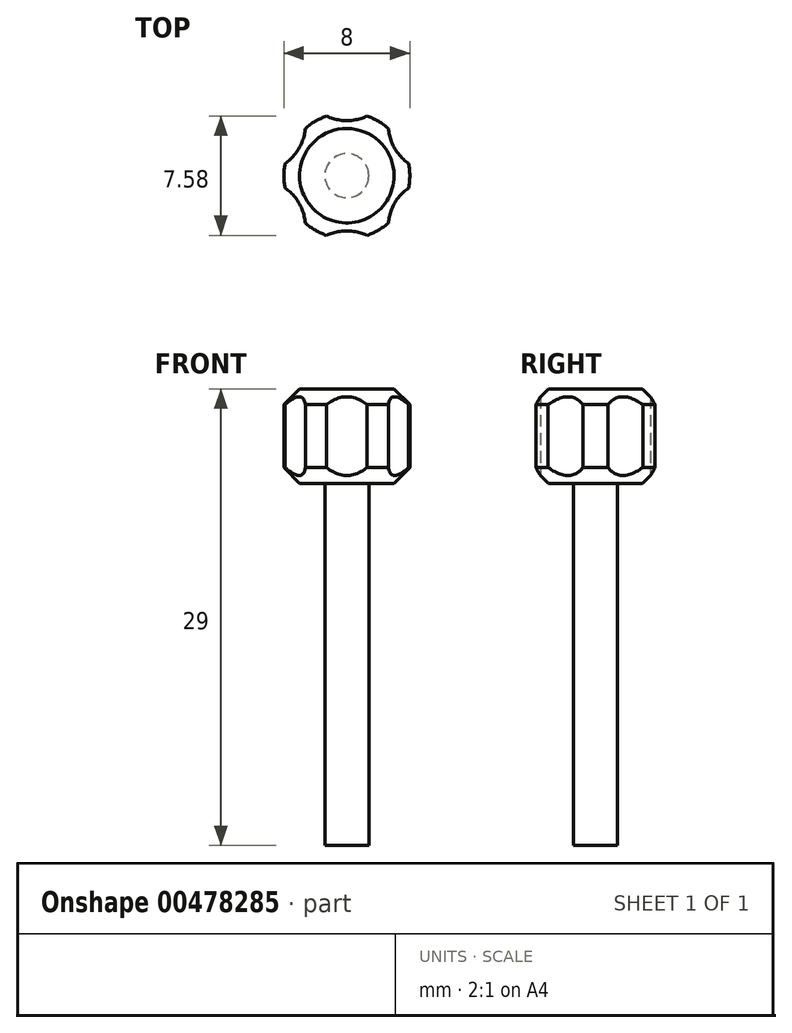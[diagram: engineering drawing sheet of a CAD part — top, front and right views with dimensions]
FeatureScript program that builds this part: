
annotation { "Feature Type Name" : "Feature", "Feature Type Description" : "" }
export const myFeature = defineFeature(function(context is Context, id is Id, definition is map)
    precondition{}
    {
        {
            var Q0;
            Q0=qCreatedBy(makeId("Top.planeOp"),FACE);
            var sketch = newSketch(context, id + "F0", { "sketchPlane" : qUnion([Q0])});
            skCircle(sketch, "E0", {"center": v(0, 0) * mm, "radius": 4 * mm});
            skCircle(sketch, "E1", {"center": v(0, 0) * mm, "radius": 1.4 * mm});
            skCircle(sketch, "E2", {"center": v(0, 6.5) * mm, "radius": 3 * mm});
            skCircle(sketch, "E3.1.0", {"center": v(-5.63, 3.25) * mm, "radius": 3 * mm});
            skCircle(sketch, "E3.2.0", {"center": v(-5.63, -3.25) * mm, "radius": 3 * mm});
            skCircle(sketch, "E3.3.0", {"center": v(0, -6.5) * mm, "radius": 3 * mm});
            skCircle(sketch, "E3.4.0", {"center": v(5.63, -3.25) * mm, "radius": 3 * mm});
            skCircle(sketch, "E3.5.0", {"center": v(5.63, 3.25) * mm, "radius": 3 * mm});
            skSolve(sketch);
        }
        {
            var Q0;
            Q0=makeQuery(id+"F0.imprint","IMPRINT",FACE,{"disambiguationData":[TD([[makeQuery(id+"F0.imprint","IMPRINT",EDGE,{"derivedFrom":sQuery(id+"F0.wireOp",EDGE,"E1")}),-1.0]])]});
            var Q1;
            Q1=makeQuery(id+"F0.imprint","IMPRINT",FACE,{"disambiguationData":[TD([[makeQuery(id+"F0.imprint","IMPRINT",EDGE,{"derivedFrom":sQuery(id+"F0.wireOp",EDGE,"E1")}),1.0]])]});
            var Q2;
            {var subQ0=sQuery(id+"F0.wireOp",EDGE,"E2");var subQ1=sQuery(id+"F0.wireOp",EDGE,"E0");var subQ2=makeQuery(id+"F0.imprint","INTERSECT",VERTEX,{"disambiguationData":[OD(0.0)],"derivedFrom":[subQ1,subQ0]});Q2=makeQuery(id+"F0.imprint","IMPRINT",FACE,{"disambiguationData":[TD([[makeQuery(id+"F0.imprint","IMPRINT",EDGE,{"disambiguationData":[TD([[subQ2,-1.0]])],"derivedFrom":subQ1}),1.0]])]});}
            var Q3;
            {var subQ0=sQuery(id+"F0.wireOp",EDGE,"E3.5.0");var subQ1=sQuery(id+"F0.wireOp",EDGE,"E0");var subQ2=makeQuery(id+"F0.imprint","INTERSECT",VERTEX,{"disambiguationData":[OD(0.0)],"derivedFrom":[subQ1,subQ0]});Q3=makeQuery(id+"F0.imprint","IMPRINT",FACE,{"disambiguationData":[TD([[makeQuery(id+"F0.imprint","IMPRINT",EDGE,{"disambiguationData":[TD([[subQ2,1.0]])],"derivedFrom":subQ1}),1.0]])]});}
            var Q4;
            {var subQ0=sQuery(id+"F0.wireOp",EDGE,"E3.4.0");var subQ1=sQuery(id+"F0.wireOp",EDGE,"E0");var subQ2=makeQuery(id+"F0.imprint","INTERSECT",VERTEX,{"disambiguationData":[OD(0.0)],"derivedFrom":[subQ1,subQ0]});Q4=makeQuery(id+"F0.imprint","IMPRINT",FACE,{"disambiguationData":[TD([[makeQuery(id+"F0.imprint","IMPRINT",EDGE,{"disambiguationData":[TD([[subQ2,-1.0]])],"derivedFrom":subQ1}),1.0]])]});}
            var Q5;
            {var subQ0=sQuery(id+"F0.wireOp",EDGE,"E3.3.0");var subQ1=sQuery(id+"F0.wireOp",EDGE,"E0");var subQ2=makeQuery(id+"F0.imprint","INTERSECT",VERTEX,{"disambiguationData":[OD(0.0)],"derivedFrom":[subQ1,subQ0]});Q5=makeQuery(id+"F0.imprint","IMPRINT",FACE,{"disambiguationData":[TD([[makeQuery(id+"F0.imprint","IMPRINT",EDGE,{"disambiguationData":[TD([[subQ2,-1.0]])],"derivedFrom":subQ1}),1.0]])]});}
            var Q6;
            {var subQ0=sQuery(id+"F0.wireOp",EDGE,"E3.2.0");var subQ1=sQuery(id+"F0.wireOp",EDGE,"E0");var subQ2=makeQuery(id+"F0.imprint","INTERSECT",VERTEX,{"disambiguationData":[OD(0.0)],"derivedFrom":[subQ1,subQ0]});Q6=makeQuery(id+"F0.imprint","IMPRINT",FACE,{"disambiguationData":[TD([[makeQuery(id+"F0.imprint","IMPRINT",EDGE,{"disambiguationData":[TD([[subQ2,-1.0]])],"derivedFrom":subQ1}),1.0]])]});}
            var Q7;
            {var subQ0=sQuery(id+"F0.wireOp",EDGE,"E3.1.0");var subQ1=sQuery(id+"F0.wireOp",EDGE,"E0");var subQ2=makeQuery(id+"F0.imprint","INTERSECT",VERTEX,{"disambiguationData":[OD(0.0)],"derivedFrom":[subQ1,subQ0]});Q7=makeQuery(id+"F0.imprint","IMPRINT",FACE,{"disambiguationData":[TD([[makeQuery(id+"F0.imprint","IMPRINT",EDGE,{"disambiguationData":[TD([[subQ2,-1.0]])],"derivedFrom":subQ1}),1.0]])]});}
            extrude(context, id + "F1", {"entities" : qUnion([Q0, Q1, Q2, Q3, Q4, Q5, Q6, Q7]), "depth" : 6 * mm});
        }
        {
            var Q0;
            Q0=makeQuery(id+"F1.opExtrude","CAP_EDGE",EDGE,{"disambiguationData":[OSD([sQuery(id+"F0.wireOp",EDGE,"E0")])],"isStart":false});
            var Q1;
            Q1=makeQuery(id+"F1.opExtrude","CAP_EDGE",EDGE,{"disambiguationData":[OSD([sQuery(id+"F0.wireOp",EDGE,"E0")])],"isStart":true});
            chamfer(context, id + "F2", {"entities" : qUnion([Q0, Q1]), "width" : 1 * mm, "tangentPropagation" : true});
        }
        {
            var Q0;
            {var subQ0=sQuery(id+"F0.wireOp",EDGE,"E3.3.0");var subQ1=sQuery(id+"F0.wireOp",EDGE,"E0");var subQ2=makeQuery(id+"F0.imprint","INTERSECT",VERTEX,{"disambiguationData":[OD(0.0)],"derivedFrom":[subQ1,subQ0]});Q0=makeQuery(id+"F0.imprint","IMPRINT",FACE,{"disambiguationData":[TD([[makeQuery(id+"F0.imprint","IMPRINT",EDGE,{"disambiguationData":[TD([[subQ2,-1.0]])],"derivedFrom":subQ1}),1.0]])]});}
            var Q1;
            {var subQ0=sQuery(id+"F0.wireOp",EDGE,"E3.2.0");var subQ1=sQuery(id+"F0.wireOp",EDGE,"E0");var subQ2=makeQuery(id+"F0.imprint","INTERSECT",VERTEX,{"disambiguationData":[OD(0.0)],"derivedFrom":[subQ1,subQ0]});Q1=makeQuery(id+"F0.imprint","IMPRINT",FACE,{"disambiguationData":[TD([[makeQuery(id+"F0.imprint","IMPRINT",EDGE,{"disambiguationData":[TD([[subQ2,-1.0]])],"derivedFrom":subQ1}),1.0]])]});}
            var Q2;
            {var subQ0=sQuery(id+"F0.wireOp",EDGE,"E3.4.0");var subQ1=sQuery(id+"F0.wireOp",EDGE,"E0");var subQ2=makeQuery(id+"F0.imprint","INTERSECT",VERTEX,{"disambiguationData":[OD(0.0)],"derivedFrom":[subQ1,subQ0]});Q2=makeQuery(id+"F0.imprint","IMPRINT",FACE,{"disambiguationData":[TD([[makeQuery(id+"F0.imprint","IMPRINT",EDGE,{"disambiguationData":[TD([[subQ2,-1.0]])],"derivedFrom":subQ1}),1.0]])]});}
            var Q3;
            {var subQ0=sQuery(id+"F0.wireOp",EDGE,"E3.5.0");var subQ1=sQuery(id+"F0.wireOp",EDGE,"E0");var subQ2=makeQuery(id+"F0.imprint","INTERSECT",VERTEX,{"disambiguationData":[OD(0.0)],"derivedFrom":[subQ1,subQ0]});Q3=makeQuery(id+"F0.imprint","IMPRINT",FACE,{"disambiguationData":[TD([[makeQuery(id+"F0.imprint","IMPRINT",EDGE,{"disambiguationData":[TD([[subQ2,1.0]])],"derivedFrom":subQ1}),1.0]])]});}
            var Q4;
            {var subQ0=sQuery(id+"F0.wireOp",EDGE,"E2");var subQ1=sQuery(id+"F0.wireOp",EDGE,"E0");var subQ2=makeQuery(id+"F0.imprint","INTERSECT",VERTEX,{"disambiguationData":[OD(0.0)],"derivedFrom":[subQ1,subQ0]});Q4=makeQuery(id+"F0.imprint","IMPRINT",FACE,{"disambiguationData":[TD([[makeQuery(id+"F0.imprint","IMPRINT",EDGE,{"disambiguationData":[TD([[subQ2,-1.0]])],"derivedFrom":subQ1}),1.0]])]});}
            var Q5;
            {var subQ0=sQuery(id+"F0.wireOp",EDGE,"E3.1.0");var subQ1=sQuery(id+"F0.wireOp",EDGE,"E0");var subQ2=makeQuery(id+"F0.imprint","INTERSECT",VERTEX,{"disambiguationData":[OD(0.0)],"derivedFrom":[subQ1,subQ0]});Q5=makeQuery(id+"F0.imprint","IMPRINT",FACE,{"disambiguationData":[TD([[makeQuery(id+"F0.imprint","IMPRINT",EDGE,{"disambiguationData":[TD([[subQ2,-1.0]])],"derivedFrom":subQ1}),1.0]])]});}
            extrude(context, id + "F3", {"entities" : qUnion([Q0, Q1, Q2, Q3, Q4, Q5]), "operationType" : NewBodyOperationType.REMOVE, "endBound" : BoundingType.THROUGH_ALL, "depth" : 25 * mm});
        }
        {
            var Q0;
            Q0=makeQuery(id+"F0.imprint","IMPRINT",FACE,{"disambiguationData":[TD([[makeQuery(id+"F0.imprint","IMPRINT",EDGE,{"derivedFrom":sQuery(id+"F0.wireOp",EDGE,"E1")}),1.0]])]});
            extrude(context, id + "F4", {"entities" : qUnion([Q0]), "operationType" : NewBodyOperationType.ADD, "oppositeDirection" : true, "depth" : 23 * mm});
        }
    });
